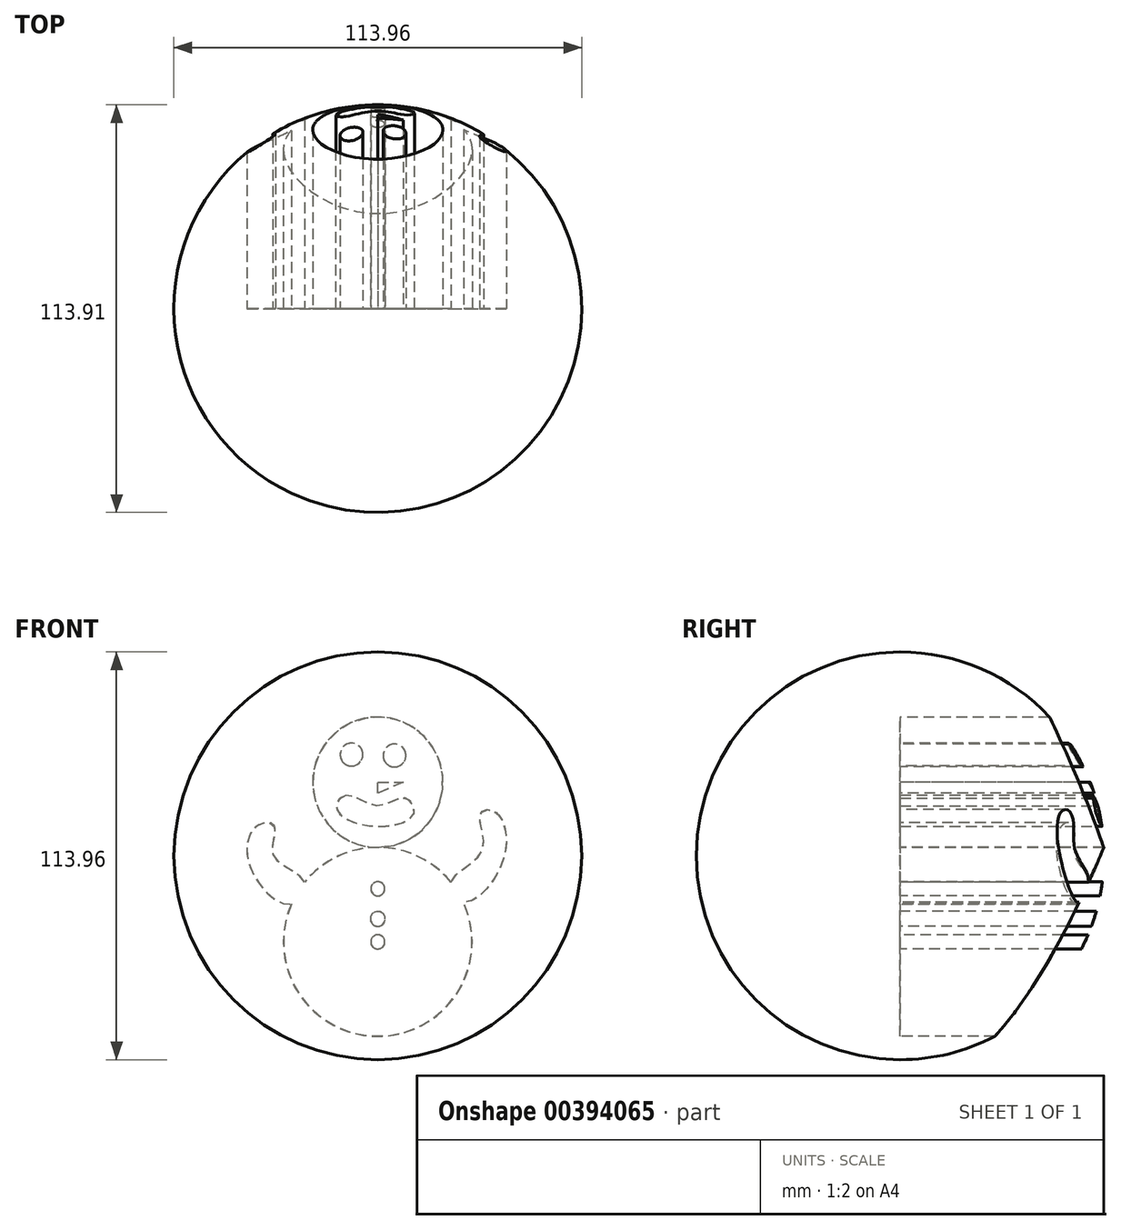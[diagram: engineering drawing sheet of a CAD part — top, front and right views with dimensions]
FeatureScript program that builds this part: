
annotation { "Feature Type Name" : "Feature", "Feature Type Description" : "" }
export const myFeature = defineFeature(function(context is Context, id is Id, definition is map)
    precondition{}
    {
        {
            var Q0;
            Q0=qCreatedBy(makeId("Front.planeOp"),FACE);
            var sketch = newSketch(context, id + "F0", { "sketchPlane" : qUnion([Q0])});
            skCircle(sketch, "E0", {"center": v(0, 0) * mm, "radius": 56.98 * mm});
            skLineSegment(sketch, "E1", {"start": v(0, -56.98) * mm, "end": v(0, 56.98) * mm});
            skSolve(sketch);
        }
        {
            var Q0;
            {var subQ0=sQuery(id+"F0.wireOp",EDGE,"E1");Q0=makeQuery(id+"F0.imprint","IMPRINT",FACE,{"disambiguationData":[TD([[makeQuery(id+"F0.imprint","IMPRINT",EDGE,{"derivedFrom":subQ0}),1.0]])]});}
            var Q1;
            Q1=sQuery(id+"F0.wireOp",EDGE,"E1");
            revolve(context, id + "F1", {"entities" : qUnion([Q0]), "axis" : qUnion([Q1]), "revolveType" : RevolveType.FULL});
        }
        {
            var Q0;
            Q0=qCreatedBy(makeId("Front.planeOp"),FACE);
            var sketch = newSketch(context, id + "F2", { "sketchPlane" : qUnion([Q0])});
            skCircle(sketch, "E2", {"center": v(0, 20.57) * mm, "radius": 18.2 * mm});
            skCircle(sketch, "E3", {"center": v(0, -24.05) * mm, "radius": 26.39 * mm});
            skLineSegment(sketch, "E4", {"start": v(-4.48, 38.22) * mm, "end": v(-15.77, 38.22) * mm});
            skLineSegment(sketch, "E5", {"start": v(-15.77, 38.22) * mm, "end": v(-15.77, 42.23) * mm});
            skLineSegment(sketch, "E6", {"start": v(-15.77, 42.23) * mm, "end": v(-5.32, 42.23) * mm});
            skLineSegment(sketch, "E7", {"start": v(-5.32, 42.23) * mm, "end": v(-5.32, 48.77) * mm});
            skLineSegment(sketch, "E8", {"start": v(-5.32, 48.77) * mm, "end": v(4.4, 48.77) * mm});
            skLineSegment(sketch, "E9", {"start": v(4.4, 48.77) * mm, "end": v(4.4, 42.23) * mm});
            skLineSegment(sketch, "E10", {"start": v(4.4, 42.23) * mm, "end": v(13.92, 42.23) * mm});
            skLineSegment(sketch, "E11", {"start": v(13.92, 42.23) * mm, "end": v(13.92, 38.22) * mm});
            skLineSegment(sketch, "E12", {"start": v(13.92, 38.22) * mm, "end": v(4.4, 38.62) * mm});
            skCircle(sketch, "E13", {"center": v(4.66, 28.04) * mm, "radius": 3.2 * mm});
            skCircle(sketch, "E14", {"center": v(-7.34, 28.29) * mm, "radius": 3.2 * mm});
            skCircle(sketch, "E15", {"center": v(0, -9.22) * mm, "radius": 1.96 * mm});
            skCircle(sketch, "E16", {"center": v(0, -17.64) * mm, "radius": 2.08 * mm});
            skCircle(sketch, "E17", {"center": v(0, -24.05) * mm, "radius": 1.96 * mm});
            skFitSpline(sketch, "E18", {"points": [v(20.44, -7.36) * mm, v(29.3, 1.7) * mm, v(28.59, 11.65) * mm, v(32.56, 12.44) * mm, v(35.38, 0) * mm, v(23.96, -13) * mm, v(20.44, -7.36) * mm]});
            skFitSpline(sketch, "E19", {"points": [v(-20.44, -7.36) * mm, v(-29.04, 0) * mm, v(-28.83, 8.29) * mm, v(-33.9, 8.28) * mm, v(-35.68, -3.07) * mm, v(-24.2, -13.51) * mm, v(-20.44, -7.36) * mm]});
            skFitSpline(sketch, "E20", {"points": [v(-8.94, 16.93) * mm, v(-11.54, 13.1) * mm, v(0, 8.23) * mm, v(10.2, 12.12) * mm, v(7.36, 16.16) * mm, v(0, 13.97) * mm, v(-8.94, 16.93) * mm]});
            skLineSegment(sketch, "E21", {"start": v(0, 20.57) * mm, "end": v(7.1, 20.57) * mm});
            skLineSegment(sketch, "E22", {"start": v(7.1, 20.57) * mm, "end": v(0, 17.46) * mm});
            skLineSegment(sketch, "E23", {"start": v(0, 17.46) * mm, "end": v(0, 20.57) * mm});
            skSolve(sketch);
        }
        {
            var Q0;
            Q0 = qSketchRegion(id + "F2", true);
            extrude(context, id + "F3", {"entities" : qUnion([Q0]), "operationType" : NewBodyOperationType.REMOVE, "oppositeDirection" : true, "depth" : 108.97 * mm});
        }
    });
